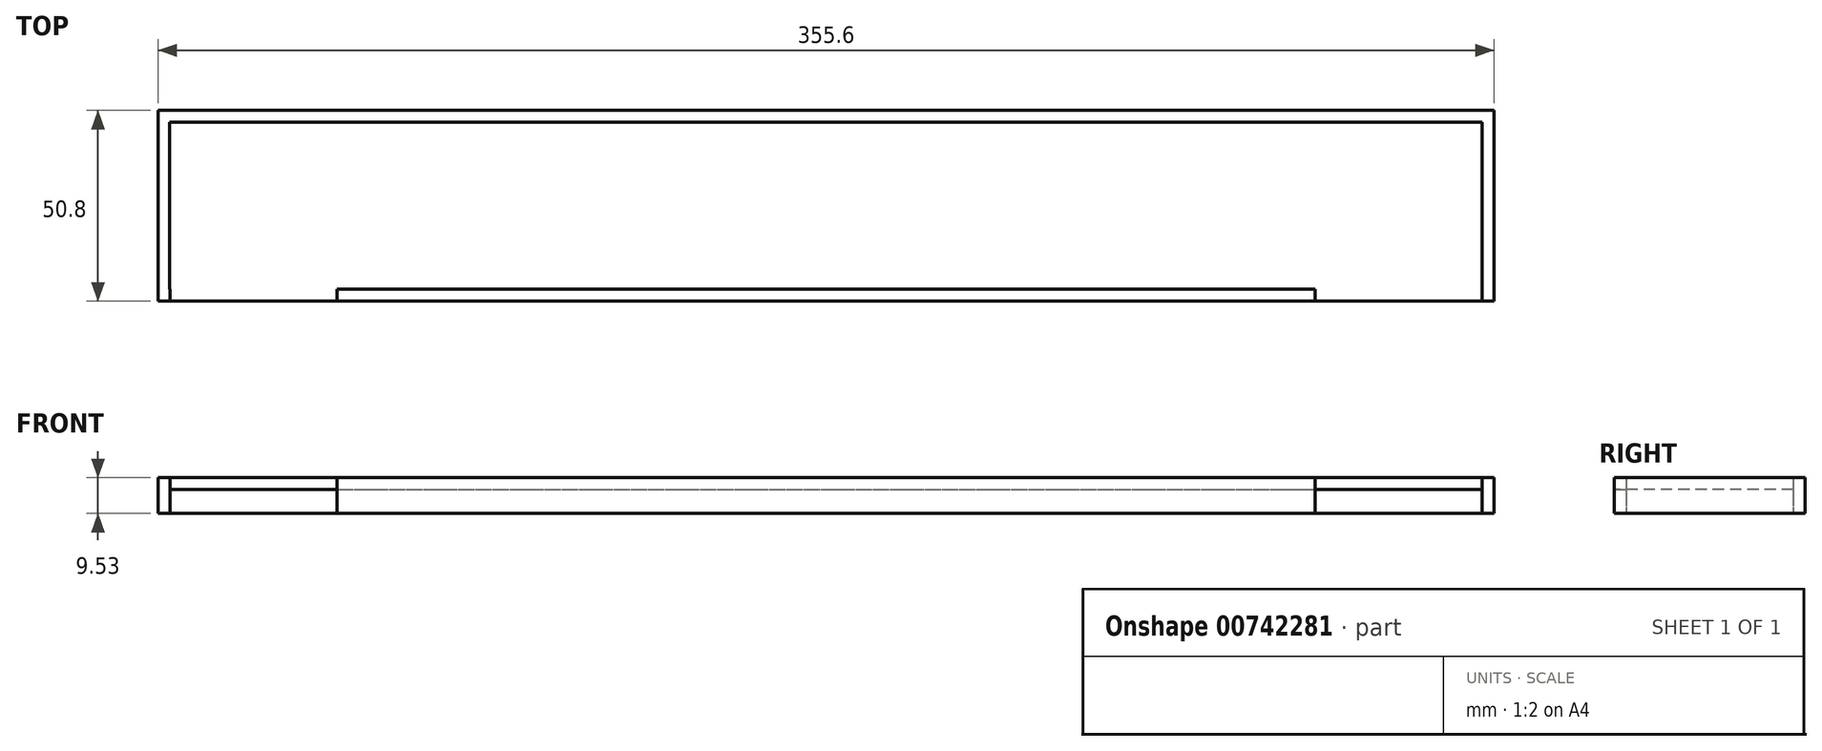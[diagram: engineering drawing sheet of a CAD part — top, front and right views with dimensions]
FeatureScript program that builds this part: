
annotation { "Feature Type Name" : "Feature", "Feature Type Description" : "" }
export const myFeature = defineFeature(function(context is Context, id is Id, definition is map)
    precondition{}
    {
        {
            var Q0;
            Q0=qCreatedBy(makeId("Top.planeOp"),FACE);
            var sketch = newSketch(context, id + "F0", { "sketchPlane" : qUnion([Q0])});
            skLineSegment(sketch, "E0.bottom", {"start": v(-187, 29.73) * mm, "end": v(168.6, 29.73) * mm});
            skLineSegment(sketch, "E0.top", {"start": v(-187, 80.53) * mm, "end": v(168.6, 80.53) * mm});
            skLineSegment(sketch, "E0.left", {"start": v(-187, 29.73) * mm, "end": v(-187, 80.53) * mm});
            skLineSegment(sketch, "E0.right", {"start": v(168.6, 29.73) * mm, "end": v(168.6, 80.53) * mm});
            skLineSegment(sketch, "E1.bottom", {"start": v(-187, 80.53) * mm, "end": v(-183.82, 80.53) * mm});
            skLineSegment(sketch, "E1.left", {"start": v(-187, 80.53) * mm, "end": v(-187, 77.35) * mm});
            skLineSegment(sketch, "E2.bottom", {"start": v(-187, 29.73) * mm, "end": v(-183.82, 29.73) * mm});
            skLineSegment(sketch, "E2.left", {"start": v(-187, 29.73) * mm, "end": v(-187, 32.9) * mm});
            skLineSegment(sketch, "E2.right", {"start": v(-183.82, 29.73) * mm, "end": v(-183.82, 32.9) * mm});
            skLineSegment(sketch, "E3.bottom", {"start": v(168.6, 29.73) * mm, "end": v(165.43, 29.73) * mm});
            skLineSegment(sketch, "E3.left", {"start": v(168.6, 29.73) * mm, "end": v(168.6, 32.9) * mm});
            skLineSegment(sketch, "E3.right", {"start": v(165.43, 29.73) * mm, "end": v(165.43, 32.9) * mm});
            skLineSegment(sketch, "E4.bottom", {"start": v(168.6, 80.53) * mm, "end": v(165.43, 80.53) * mm});
            skLineSegment(sketch, "E4.left", {"start": v(168.6, 80.53) * mm, "end": v(168.6, 77.35) * mm});
            skLineSegment(sketch, "E5.bottom", {"start": v(-183.99, 77.35) * mm, "end": v(165.43, 77.35) * mm});
            skLineSegment(sketch, "E5.top", {"start": v(-183.99, 32.9) * mm, "end": v(165.43, 32.9) * mm});
            skLineSegment(sketch, "E5.left", {"start": v(-183.99, 77.35) * mm, "end": v(-183.99, 32.9) * mm});
            skLineSegment(sketch, "E5.right", {"start": v(165.43, 77.35) * mm, "end": v(165.43, 32.9) * mm});
            skLineSegment(sketch, "E6.bottom", {"start": v(-187, 29.73) * mm, "end": v(-136.2, 29.73) * mm});
            skLineSegment(sketch, "E7.bottom", {"start": v(168.6, 29.73) * mm, "end": v(117.8, 29.73) * mm});
            skLineSegment(sketch, "E8.bottom", {"start": v(-136.2, 29.73) * mm, "end": v(-139.37, 29.73) * mm});
            skLineSegment(sketch, "E8.top", {"start": v(-136.2, 32.9) * mm, "end": v(-139.37, 32.9) * mm});
            skLineSegment(sketch, "E8.right", {"start": v(-139.37, 29.73) * mm, "end": v(-139.37, 32.9) * mm});
            skLineSegment(sketch, "E9.bottom", {"start": v(117.8, 29.73) * mm, "end": v(120.98, 29.73) * mm});
            skLineSegment(sketch, "E9.top", {"start": v(117.8, 32.9) * mm, "end": v(120.98, 32.9) * mm});
            skLineSegment(sketch, "E9.right", {"start": v(120.98, 29.73) * mm, "end": v(120.98, 32.9) * mm});
            skSolve(sketch);
        }
        {
            var Q0;
            Q0=makeQuery(id+"F0.imprint","IMPRINT",FACE,{"disambiguationData":[TD([[makeQuery(id+"F0.imprint","IMPRINT",EDGE,{"derivedFrom":sQuery(id+"F0.wireOp",EDGE,"E0.top")}),-1.0]])]});
            var Q1;
            Q1=makeQuery(id+"F0.imprint","IMPRINT",FACE,{"disambiguationData":[TD([[makeQuery(id+"F0.imprint","IMPRINT",EDGE,{"derivedFrom":sQuery(id+"F0.wireOp",EDGE,"E0.bottom")}),1.0]])]});
            extrude(context, id + "F1", {"entities" : qUnion([Q0, Q1]), "depth" : 9.52 * mm, "offsetDistance" : 25.4 * mm});
        }
        {
            var Q0;
            Q0=makeQuery(id+"F0.imprint","IMPRINT",FACE,{"disambiguationData":[TD([[makeQuery(id+"F0.imprint","IMPRINT",EDGE,{"derivedFrom":sQuery(id+"F0.wireOp",EDGE,"E5.bottom")}),-1.0]])]});
            var Q1;
            {var subQ0=sQuery(id+"F0.wireOp",EDGE,"E2.right");Q1=makeQuery(id+"F0.imprint","IMPRINT",FACE,{"disambiguationData":[TD([[makeQuery(id+"F0.imprint","IMPRINT",EDGE,{"derivedFrom":subQ0}),-1.0]])]});}
            var Q2;
            {var subQ0=sQuery(id+"F0.wireOp",EDGE,"E3.right");Q2=makeQuery(id+"F0.imprint","IMPRINT",FACE,{"disambiguationData":[TD([[makeQuery(id+"F0.imprint","IMPRINT",EDGE,{"derivedFrom":subQ0}),1.0]])]});}
            extrude(context, id + "F2", {"entities" : qUnion([Q0, Q1, Q2]), "depth" : 6.35 * mm, "offsetDistance" : 25.4 * mm});
        }
    });
